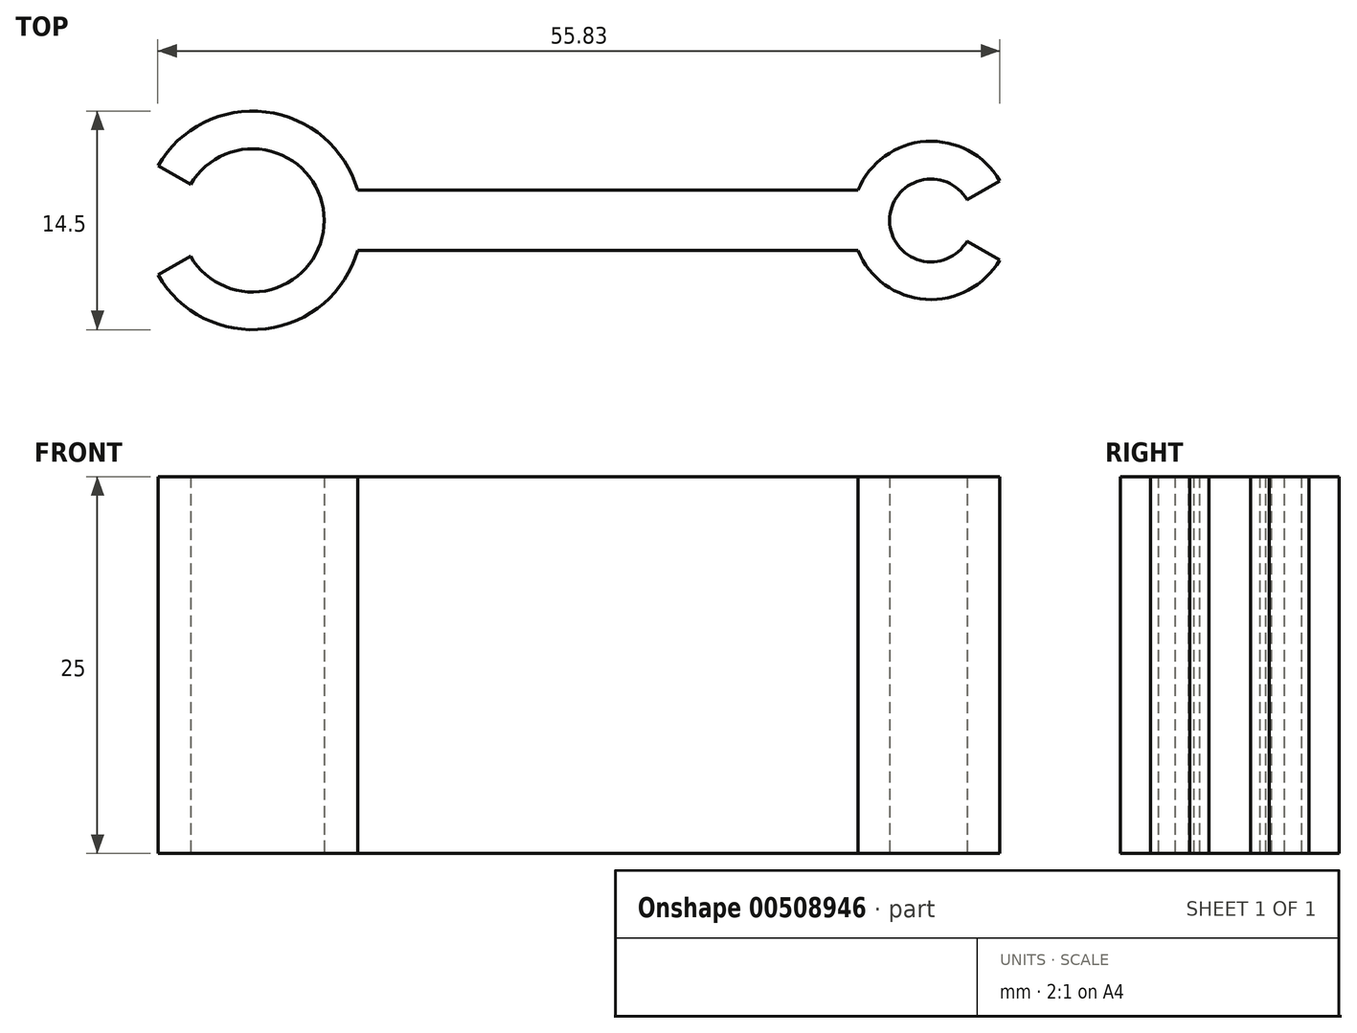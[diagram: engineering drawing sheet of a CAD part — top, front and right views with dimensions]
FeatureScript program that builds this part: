
annotation { "Feature Type Name" : "Feature", "Feature Type Description" : "" }
export const myFeature = defineFeature(function(context is Context, id is Id, definition is map)
    precondition{}
    {
        {
            var Q0;
            Q0=qCreatedBy(makeId("Top.planeOp"),FACE);
            var sketch = newSketch(context, id + "F0", { "sketchPlane" : qUnion([Q0])});
            skArc(sketch, "E0", {"start": v(-4.11, -2.37) * mm, "mid": v(4.75, 0) * mm, "end": v(-4.11, 2.38) * mm});
            skArc(sketch, "E1", {"start": v(-6.28, -3.62) * mm, "mid": v(0.88, -7.2) * mm, "end": v(6.97, -2) * mm});
            skArc(sketch, "E2", {"start": v(47.38, 1.38) * mm, "mid": v(42.25, 0) * mm, "end": v(47.38, -1.38) * mm});
            skArc(sketch, "E3", {"start": v(49.55, 2.63) * mm, "mid": v(44.65, 5.24) * mm, "end": v(40.15, 2) * mm});
            skLineSegment(sketch, "E4.0", {"start": v(6.97, -2) * mm, "end": v(40.15, -2) * mm});
            skLineSegment(sketch, "E5.0", {"start": v(6.97, 2) * mm, "end": v(40.15, 2) * mm});
            skLineSegment(sketch, "E6", {"start": v(-4.11, 2.37) * mm, "end": v(-6.28, 3.63) * mm});
            skLineSegment(sketch, "E7", {"start": v(-6.28, -3.62) * mm, "end": v(-4.11, -2.38) * mm});
            skLineSegment(sketch, "E8", {"start": v(47.38, 1.38) * mm, "end": v(49.55, 2.63) * mm});
            skLineSegment(sketch, "E9", {"start": v(47.38, -1.37) * mm, "end": v(49.55, -2.62) * mm});
            skArc(sketch, "E10.trimOffspring", {"start": v(40.15, -2) * mm, "mid": v(44.65, -5.24) * mm, "end": v(49.55, -2.62) * mm});
            skArc(sketch, "E11.trimOffspring", {"start": v(6.97, 2) * mm, "mid": v(0.88, 7.2) * mm, "end": v(-6.28, 3.63) * mm});
            skSolve(sketch);
        }
        {
            var Q0;
            Q0=makeQuery(id+"F0.imprint","IMPRINT",FACE,{"disambiguationData":[TD([[makeQuery(id+"F0.imprint","IMPRINT",EDGE,{"derivedFrom":sQuery(id+"F0.wireOp",EDGE,"E0")}),-1.0]])]});
            extrude(context, id + "F1", {"entities" : qUnion([Q0]), "depth" : 25 * mm});
        }
    });
